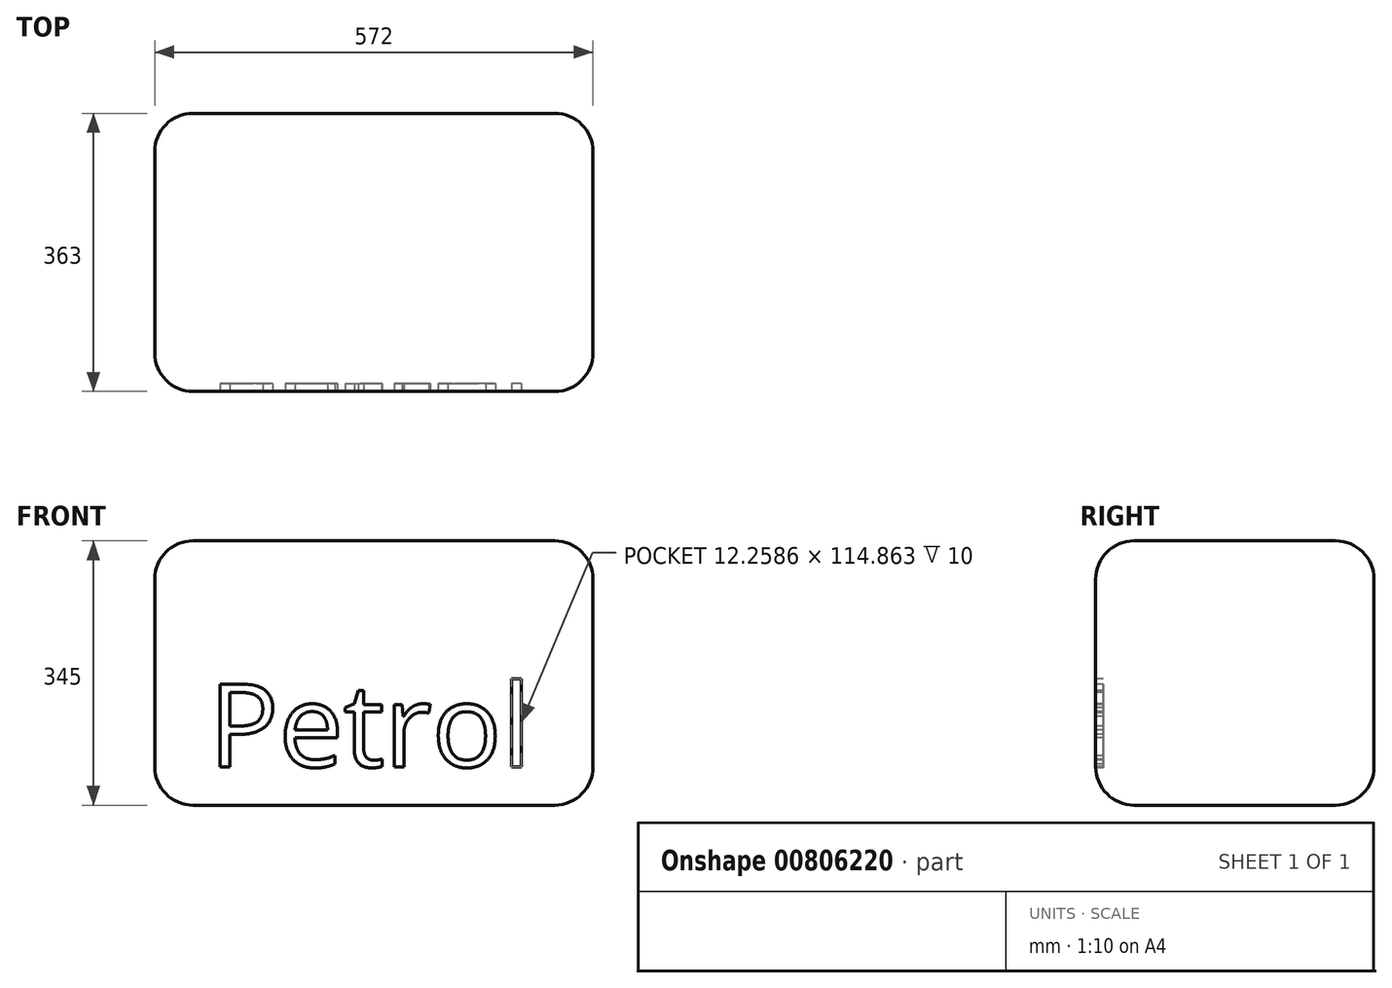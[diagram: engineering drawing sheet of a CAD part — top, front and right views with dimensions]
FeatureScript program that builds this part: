
annotation { "Feature Type Name" : "Feature", "Feature Type Description" : "" }
export const myFeature = defineFeature(function(context is Context, id is Id, definition is map)
    precondition{}
    {
        {
            var Q0;
            Q0=qCreatedBy(makeId("Front.planeOp"),FACE);
            var sketch = newSketch(context, id + "F0", { "sketchPlane" : qUnion([Q0])});
            skLineSegment(sketch, "E0.bottom", {"start": v(286, -172.5) * mm, "end": v(-286, -172.5) * mm});
            skLineSegment(sketch, "E0.top", {"start": v(286, 172.5) * mm, "end": v(-286, 172.5) * mm});
            skLineSegment(sketch, "E0.left", {"start": v(286, -172.5) * mm, "end": v(286, 172.5) * mm});
            skLineSegment(sketch, "E0.right", {"start": v(-286, -172.5) * mm, "end": v(-286, 172.5) * mm});
            skPoint(sketch, "E0.middle", {"position": v(0, 0) * mm});
            skSolve(sketch);
        }
        {
            var Q0;
            Q0=qSketchRegion(id+"F0",true);
            extrude(context, id + "F1", {"entities" : qUnion([Q0]), "depth" : 363 * mm, "offsetDistance" : 25 * mm});
        }
        {
            var Q0;
            Q0=makeQuery(id+"F1.opExtrude","CAP_FACE",FACE,{"disambiguationData":[OSD([sQuery(id+"F0.wireOp",EDGE,"E0.bottom"),sQuery(id+"F0.wireOp",EDGE,"E0.top"),sQuery(id+"F0.wireOp",EDGE,"E0.left"),sQuery(id+"F0.wireOp",EDGE,"E0.right")])],"isStart":false});
            var Q1;
            Q1=makeQuery(id+"F1.opExtrude","SWEPT_EDGE",EDGE,{"disambiguationData":[OSD([sQuery(id+"F0.wireOp",EDGE,"E0.bottom"),sQuery(id+"F0.wireOp",EDGE,"E0.left")])]});
            var Q2;
            Q2=makeQuery(id+"F1.opExtrude","SWEPT_EDGE",EDGE,{"disambiguationData":[OSD([sQuery(id+"F0.wireOp",EDGE,"E0.top"),sQuery(id+"F0.wireOp",EDGE,"E0.left")])]});
            var Q3;
            Q3=makeQuery(id+"F1.opExtrude","SWEPT_EDGE",EDGE,{"disambiguationData":[OSD([sQuery(id+"F0.wireOp",EDGE,"E0.top"),sQuery(id+"F0.wireOp",EDGE,"E0.right")])]});
            var Q4;
            Q4=makeQuery(id+"F1.opExtrude","CAP_EDGE",EDGE,{"disambiguationData":[OSD([sQuery(id+"F0.wireOp",EDGE,"E0.bottom")])],"isStart":false});
            var Q5;
            Q5=makeQuery(id+"F1.opExtrude","CAP_EDGE",EDGE,{"disambiguationData":[OSD([sQuery(id+"F0.wireOp",EDGE,"E0.top")])],"isStart":true});
            var Q6;
            Q6=makeQuery(id+"F1.opExtrude","CAP_EDGE",EDGE,{"disambiguationData":[OSD([sQuery(id+"F0.wireOp",EDGE,"E0.top")])],"isStart":false});
            var Q7;
            Q7=makeQuery(id+"F1.opExtrude","SWEPT_EDGE",EDGE,{"disambiguationData":[OSD([sQuery(id+"F0.wireOp",EDGE,"E0.bottom"),sQuery(id+"F0.wireOp",EDGE,"E0.right")])]});
            var Q8;
            Q8=makeQuery(id+"F1.opExtrude","CAP_EDGE",EDGE,{"disambiguationData":[OSD([sQuery(id+"F0.wireOp",EDGE,"E0.bottom")])],"isStart":true});
            var Q9;
            Q9=makeQuery(id+"F1.opExtrude","CAP_EDGE",EDGE,{"disambiguationData":[OSD([sQuery(id+"F0.wireOp",EDGE,"E0.left")])],"isStart":true});
            var Q10;
            Q10=makeQuery(id+"F1.opExtrude","CAP_EDGE",EDGE,{"disambiguationData":[OSD([sQuery(id+"F0.wireOp",EDGE,"E0.left")])],"isStart":false});
            var Q11;
            Q11=makeQuery(id+"F1.opExtrude","CAP_EDGE",EDGE,{"disambiguationData":[OSD([sQuery(id+"F0.wireOp",EDGE,"E0.right")])],"isStart":true});
            var Q12;
            Q12=makeQuery(id+"F1.opExtrude","CAP_EDGE",EDGE,{"disambiguationData":[OSD([sQuery(id+"F0.wireOp",EDGE,"E0.right")])],"isStart":false});
            fillet(context, id + "F2", {"entities" : qUnion([Q0, Q1, Q2, Q3, Q4, Q5, Q6, Q7, Q8, Q9, Q10, Q11, Q12]), "radius" : 50 * mm, "tangentPropagation" : true, "allowEdgeOverflow" : false});
        }
        {
            var Q0;
            Q0=makeQuery(id+"F1.opExtrude","CAP_FACE",FACE,{"disambiguationData":[OSD([sQuery(id+"F0.wireOp",EDGE,"E0.bottom"),sQuery(id+"F0.wireOp",EDGE,"E0.top"),sQuery(id+"F0.wireOp",EDGE,"E0.left"),sQuery(id+"F0.wireOp",EDGE,"E0.right")])],"isStart":false});
            var sketch = newSketch(context, id + "F3", { "sketchPlane" : qUnion([Q0])});
            skText(sketch, "E1", { "text": "Petrol", "fontName": "OpenSans-Regular.ttf"});
            const initialGuessF3  = {"E1": [-0.2153, -0.1225, 1, 0, 0.10884]};
            skSetInitialGuess(sketch, initialGuessF3);
            skSolve(sketch);
        }
        {
            var Q0;
            Q0=qSketchRegion(id+"F3",true);
            extrude(context, id + "F4", {"entities" : qUnion([Q0]), "operationType" : NewBodyOperationType.REMOVE, "oppositeDirection" : true, "depth" : 10 * mm, "offsetDistance" : 25 * mm});
        }
    });
